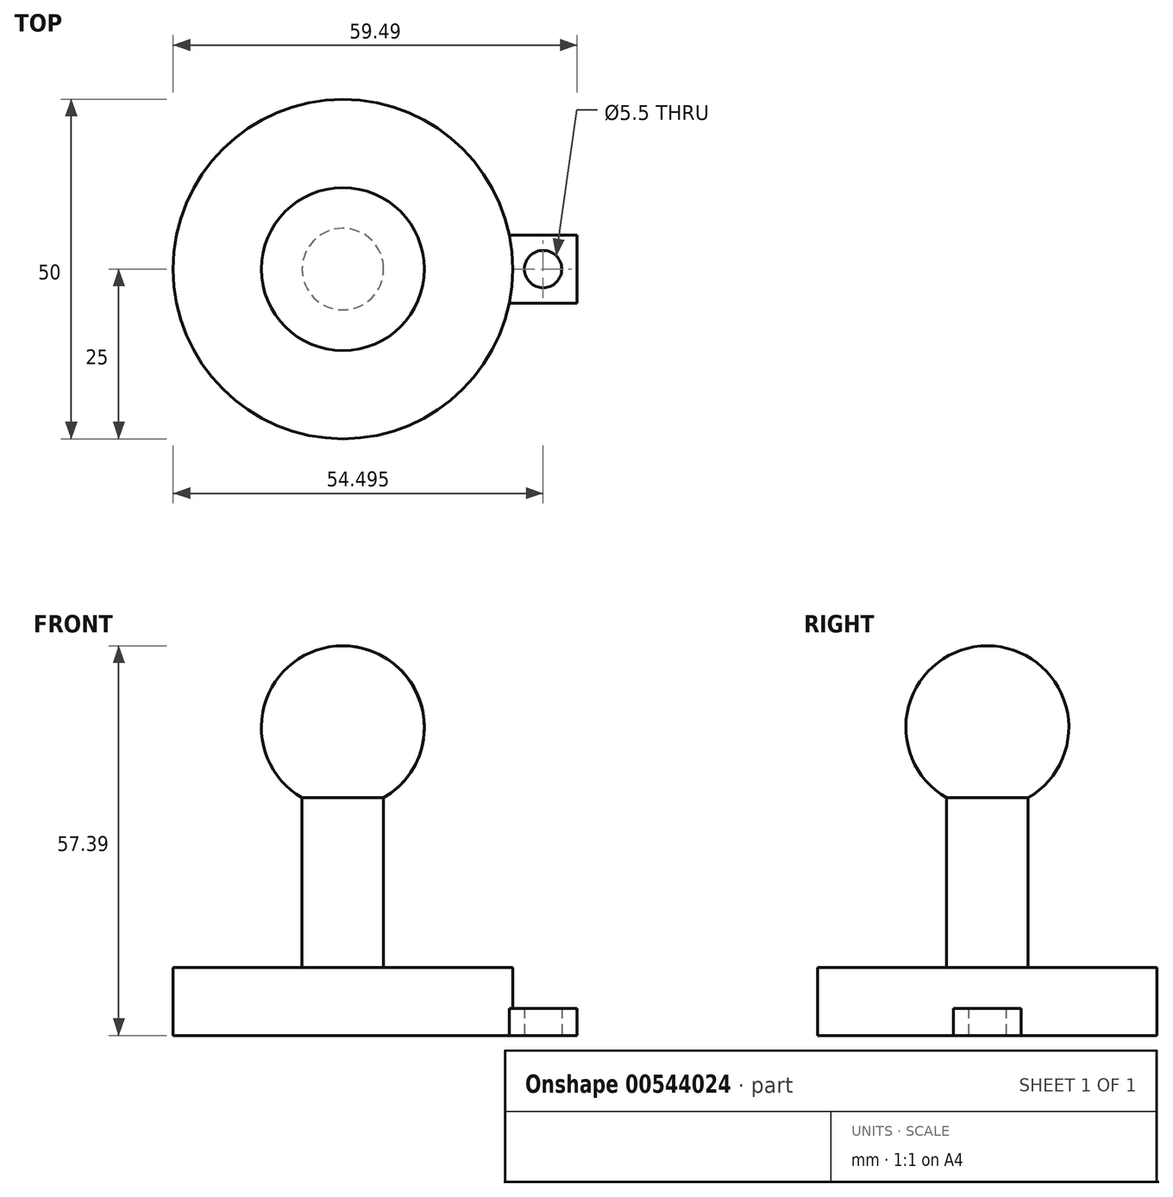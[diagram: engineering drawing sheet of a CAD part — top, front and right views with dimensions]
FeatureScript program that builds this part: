
annotation { "Feature Type Name" : "Feature", "Feature Type Description" : "" }
export const myFeature = defineFeature(function(context is Context, id is Id, definition is map)
    precondition{}
    {
        {
            var Q0;
            Q0=qCreatedBy(makeId("Front.planeOp"),FACE);
            var sketch = newSketch(context, id + "F0", { "sketchPlane" : qUnion([Q0])});
            skLineSegment(sketch, "E0", {"start": v(6, 10) * mm, "end": v(6, 35) * mm});
            skArc(sketch, "E1", {"start": v(6, 35) * mm, "mid": v(11.6, 48.5) * mm, "end": v(0, 57.4) * mm});
            skLineSegment(sketch, "E2", {"start": v(6, 10) * mm, "end": v(25, 10) * mm});
            skLineSegment(sketch, "E3", {"start": v(25, 10) * mm, "end": v(25, 0) * mm});
            skLineSegment(sketch, "E4", {"start": v(25, 0) * mm, "end": v(0, 0) * mm});
            skLineSegment(sketch, "E5", {"start": v(0, 57.4) * mm, "end": v(0, 0) * mm});
            skSolve(sketch);
        }
        {
            var Q0;
            Q0=makeQuery(id+"F0.imprint","IMPRINT",FACE,{"disambiguationData":[TD([[makeQuery(id+"F0.imprint","IMPRINT",EDGE,{"derivedFrom":sQuery(id+"F0.wireOp",EDGE,"E0")}),1.0]])]});
            var Q1;
            Q1=sQuery(id+"F0.wireOp",EDGE,"E5");
            revolve(context, id + "F1", {"entities" : qUnion([Q0]), "axis" : qUnion([Q1]), "revolveType" : RevolveType.FULL});
        }
        {
            var Q0;
            Q0=makeQuery(id+"F1.opRevolve","SWEPT_FACE",FACE,{"disambiguationData":[OSD([sQuery(id+"F0.wireOp",EDGE,"E4")])]});
            var sketch = newSketch(context, id + "F2", { "sketchPlane" : qUnion([Q0])});
            skLineSegment(sketch, "E6.bottom", {"start": v(24.5, 5) * mm, "end": v(34.5, 5) * mm});
            skLineSegment(sketch, "E6.top", {"start": v(24.5, -5) * mm, "end": v(34.5, -5) * mm});
            skLineSegment(sketch, "E6.left", {"start": v(24.5, 5) * mm, "end": v(24.5, -5) * mm});
            skLineSegment(sketch, "E6.right", {"start": v(34.5, 5) * mm, "end": v(34.5, -5) * mm});
            skCircle(sketch, "E7", {"center": v(29.5, 0) * mm, "radius": 2.75 * mm});
            skPoint(sketch, "E7.centerSnap0", {"position": v(29.5, 5) * mm});
            skPoint(sketch, "E7.centerSnap1", {"position": v(34.5, 0) * mm});
            skSolve(sketch);
        }
        {
            var Q0;
            Q0 = qSketchRegion(id + "F2", true);
            extrude(context, id + "F3", {"entities" : qUnion([Q0]), "operationType" : NewBodyOperationType.ADD, "oppositeDirection" : true, "depth" : 4 * mm, "offsetDistance" : 25 * mm});
        }
    });
